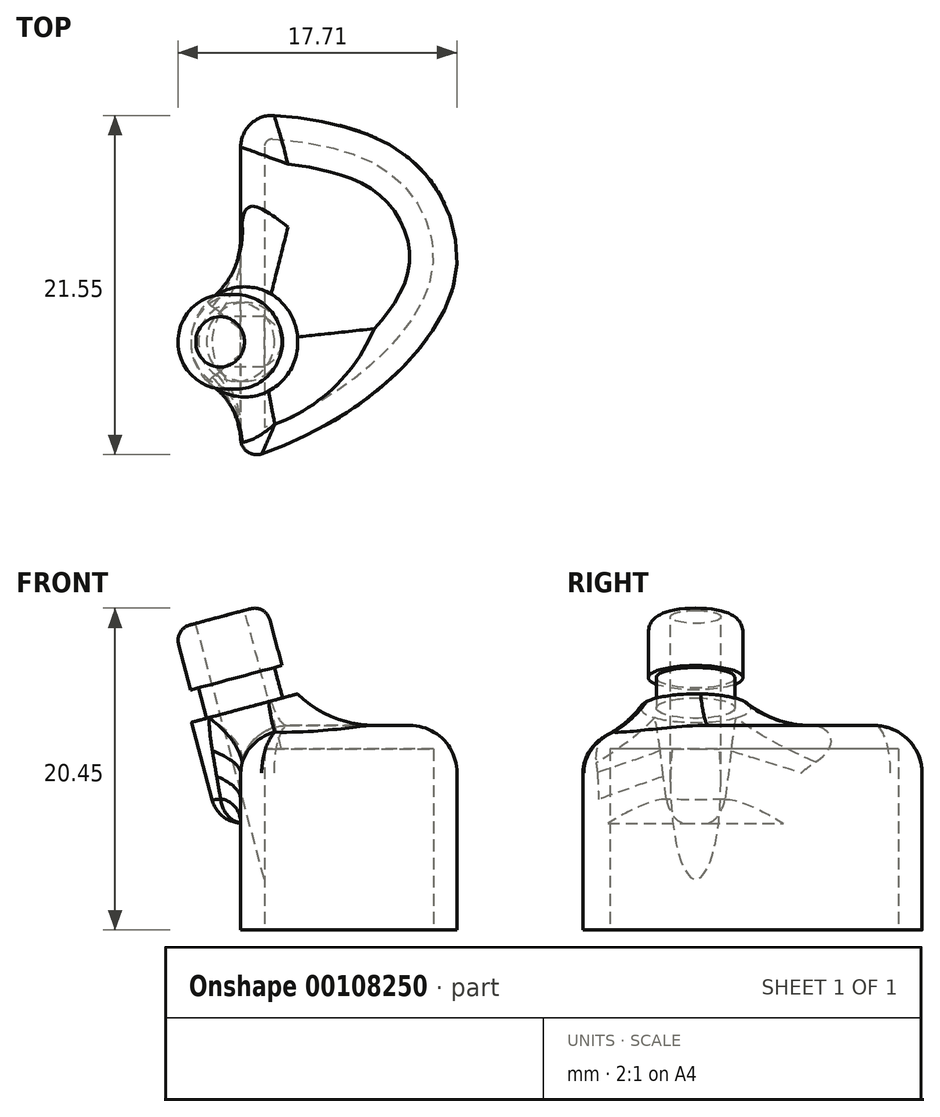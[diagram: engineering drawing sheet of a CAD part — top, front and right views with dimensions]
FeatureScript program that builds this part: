
annotation { "Feature Type Name" : "Feature", "Feature Type Description" : "" }
export const myFeature = defineFeature(function(context is Context, id is Id, definition is map)
    precondition{}
    {
        {
            var Q0;
            Q0=qCreatedBy(makeId("Top.planeOp"),FACE);
            var sketch = newSketch(context, id + "F0", { "sketchPlane" : qUnion([Q0])});
            skLineSegment(sketch, "E0", {"start": v(0, 10.03) * mm, "end": v(0, -11.97) * mm});
            skFitSpline(sketch, "E1", {"points": [v(0, 10.03) * mm, v(10.47, 7.41) * mm, v(13.67, 0) * mm, v(8.71, -7.47) * mm, v(0, -11.97) * mm], "startDerivative": vector(40.6, -0.18) * mm, "endDerivative": vector(-39.36, -12.15) * mm});
            skSolve(sketch);
        }
        {
            var Q0;
            Q0=makeQuery(id+"F0.imprint","IMPRINT",FACE,{"disambiguationData":[TD([[makeQuery(id+"F0.imprint","IMPRINT",EDGE,{"derivedFrom":sQuery(id+"F0.wireOp",EDGE,"E0")}),1.0]])]});
            extrude(context, id + "F1", {"entities" : qUnion([Q0]), "depth" : 13 * mm});
        }
        {
            var Q0;
            {var subQ0=sQuery(id+"F0.wireOp",EDGE,"E1");var subQ1=sQuery(id+"F0.wireOp",EDGE,"E0");Q0=makeQuery(id+"F1.opExtrude","SWEPT_EDGE",EDGE,{"disambiguationData":[OSD([subQ1,subQ0]),TDD([makeQuery(id+"F0.imprint","INTERSECT",VERTEX,{"disambiguationData":[OD(0.0)],"derivedFrom":[subQ1,subQ0]})])]});}
            fillet(context, id + "F2", {"entities" : qUnion([Q0]), "radius" : 2 * mm, "tangentPropagation" : true, "allowEdgeOverflow" : false});
        }
        {
            var Q0;
            {var subQ0=sQuery(id+"F0.wireOp",EDGE,"E1");var subQ1=sQuery(id+"F0.wireOp",EDGE,"E0");Q0=makeQuery(id+"F1.opExtrude","SWEPT_EDGE",EDGE,{"disambiguationData":[OSD([subQ1,subQ0]),TDD([makeQuery(id+"F0.imprint","INTERSECT",VERTEX,{"disambiguationData":[OD(1.0)],"derivedFrom":[subQ1,subQ0]})])]});}
            fillet(context, id + "F3", {"entities" : qUnion([Q0]), "radius" : 1 * mm, "tangentPropagation" : true, "allowEdgeOverflow" : false});
        }
        {
            var Q0;
            Q0=makeQuery(id+"F1.opExtrude","CAP_FACE",FACE,{"disambiguationData":[OSD([sQuery(id+"F0.wireOp",EDGE,"E0"),sQuery(id+"F0.wireOp",EDGE,"E1")])],"isStart":false});
            var Q1;
            Q1=makeQuery(id+"F1.opExtrude","CAP_EDGE",EDGE,{"disambiguationData":[OSD([sQuery(id+"F0.wireOp",EDGE,"E0")])],"isStart":false});
            cPlane(context, id + "F4", {"entities" : qUnion([Q0, Q1]), "cplaneType" : CPlaneType.LINE_ANGLE, "offset" : 25 * mm, "angle" : 15 * degree, "width" : 150 * mm, "height" : 150 * mm});
        }
        {
            var Q0;
            Q0=makeQuery(id+"F1.opExtrude","CAP_FACE",FACE,{"disambiguationData":[OSD([sQuery(id+"F0.wireOp",EDGE,"E0"),sQuery(id+"F0.wireOp",EDGE,"E1")])],"isStart":true});
            shell(context, id + "F5", {"entities" : qUnion([Q0]), "thickness" : 1.5 * mm});
        }
        {
            var Q0;
            Q0=qCreatedBy(id+"F4.planeOp",FACE);
            var sketch = newSketch(context, id + "F6", { "sketchPlane" : qUnion([Q0])});
            skLineSegment(sketch, "E2", {"start": v(-1.22, 10.68) * mm, "end": v(-1.22, 3.68) * mm});
            skCircle(sketch, "E3", {"center": v(3.89, 4.42) * mm, "radius": 3.5 * mm});
            skSolve(sketch);
        }
        {
            var Q0;
            Q0=makeQuery(id+"F6.imprint","IMPRINT",FACE,{"disambiguationData":[TD([[makeQuery(id+"F6.imprint","IMPRINT",EDGE,{"derivedFrom":sQuery(id+"F6.wireOp",EDGE,"E3")}),1.0]])]});
            extrude(context, id + "F7", {"entities" : qUnion([Q0]), "operationType" : NewBodyOperationType.ADD, "depth" : 6 * mm});
        }
        {
            var Q0;
            Q0=makeQuery(id+"F1.opExtrude","CAP_FACE",FACE,{"disambiguationData":[OSD([sQuery(id+"F0.wireOp",EDGE,"E0"),sQuery(id+"F0.wireOp",EDGE,"E1")])],"isStart":true});
            var sketch = newSketch(context, id + "F8", { "sketchPlane" : qUnion([Q0])});
            skLineSegment(sketch, "E4", {"start": v(1.5, 9.87) * mm, "end": v(1.5, -2.54) * mm});
            skLineSegment(sketch, "E5", {"start": v(1.5, -2.54) * mm, "end": v(10.54, -1.4) * mm});
            skLineSegment(sketch, "E6", {"start": v(10.54, -1.4) * mm, "end": v(8.02, 6.1) * mm});
            skLineSegment(sketch, "E7", {"start": v(8.02, 6.1) * mm, "end": v(1.5, 9.87) * mm});
            skSolve(sketch);
        }
        {
            var Q0;
            Q0=makeQuery(id+"F8.imprint","IMPRINT",FACE,{"disambiguationData":[TD([[makeQuery(id+"F8.imprint","IMPRINT",EDGE,{"derivedFrom":sQuery(id+"F8.wireOp",EDGE,"E4")}),-1.0]])]});
            extrude(context, id + "F9", {"entities" : qUnion([Q0]), "operationType" : NewBodyOperationType.REMOVE, "oppositeDirection" : true, "depth" : 11.5 * mm});
        }
        {
            var Q0;
            Q0=makeQuery(id+"F7.opExtrude","CAP_FACE",FACE,{"disambiguationData":[OSD([sQuery(id+"F6.wireOp",EDGE,"E3")])],"isStart":true});
            extrude(context, id + "F10", {"entities" : qUnion([Q0]), "operationType" : NewBodyOperationType.ADD, "depth" : 1 * mm});
        }
        {
            var Q0;
            Q0=makeQuery(id+"F10.opExtrude","CAP_FACE",FACE,{"disambiguationData":[OSD([sQuery(id+"F6.wireOp",EDGE,"E3")])],"isStart":false});
            var sketch = newSketch(context, id + "F11", { "sketchPlane" : qUnion([Q0])});
            skCircle(sketch, "E8", {"center": v(3.89, -4.42) * mm, "radius": 2.5 * mm});
            skSolve(sketch);
        }
        {
            var Q0;
            Q0=makeQuery(id+"F11.imprint","IMPRINT",FACE,{"disambiguationData":[TD([[makeQuery(id+"F11.imprint","IMPRINT",EDGE,{"derivedFrom":sQuery(id+"F11.wireOp",EDGE,"E8")}),1.0]])]});
            extrude(context, id + "F12", {"entities" : qUnion([Q0]), "operationType" : NewBodyOperationType.ADD, "depth" : 2 * mm});
        }
        {
            var Q0;
            Q0=makeQuery(id+"F12.opExtrude","CAP_FACE",FACE,{"disambiguationData":[OSD([sQuery(id+"F11.wireOp",EDGE,"E8")])],"isStart":false});
            var sketch = newSketch(context, id + "F13", { "sketchPlane" : qUnion([Q0])});
            skCircle(sketch, "E9", {"center": v(3.89, -4.42) * mm, "radius": 3 * mm});
            skSolve(sketch);
        }
        {
            var Q0;
            Q0 = qSketchRegion(id + "F13", true);
            extrude(context, id + "F14", {"entities" : qUnion([Q0]), "operationType" : NewBodyOperationType.ADD, "depth" : 4 * mm});
        }
        {
            var Q0;
            Q0=makeQuery(id+"F14.opExtrude","CAP_EDGE",EDGE,{"disambiguationData":[OSD([sQuery(id+"F13.wireOp",EDGE,"E9")])],"isStart":false});
            fillet(context, id + "F15", {"entities" : qUnion([Q0]), "radius" : 1 * mm, "tangentPropagation" : true, "allowEdgeOverflow" : false});
        }
        {
            var Q0;
            Q0=makeQuery(id+"F1.opExtrude","CAP_EDGE",EDGE,{"disambiguationData":[OSD([sQuery(id+"F0.wireOp",EDGE,"E1")])],"isStart":false});
            fillet(context, id + "F16", {"entities" : qUnion([Q0]), "radius" : 3 * mm, "tangentPropagation" : true, "allowEdgeOverflow" : false});
        }
        {
            var Q0;
            Q0=makeQuery(id+"F7.boolean.opBoolean","INTERSECT",EDGE,{"derivedFrom":[makeQuery(id+"F1.opExtrude","CAP_FACE",FACE,{"disambiguationData":[OSD([sQuery(id+"F0.wireOp",EDGE,"E0"),sQuery(id+"F0.wireOp",EDGE,"E1")])],"isStart":false}),makeQuery(id+"F7.opExtrude","SWEPT_FACE",FACE,{"disambiguationData":[OSD([sQuery(id+"F6.wireOp",EDGE,"E3")])]})]});
            fillet(context, id + "F17", {"entities" : qUnion([Q0]), "radius" : 7 * mm, "tangentPropagation" : true, "allowEdgeOverflow" : false});
        }
        {
            var Q0;
            {var subQ0=sQuery(id+"F6.wireOp",EDGE,"E3");Q0=makeQuery(id+"F7.boolean.opBoolean","SPLIT",EDGE,{"disambiguationData":[TD([makeQuery(id+"F1.opExtrude","SWEPT_FACE",FACE,{"disambiguationData":[OSD([sQuery(id+"F0.wireOp",EDGE,"E0")])]})])],"derivedFrom":makeQuery(id+"F7.opExtrude","CAP_EDGE",EDGE,{"disambiguationData":[OSD([subQ0])],"isStart":false})});}
            fillet(context, id + "F18", {"entities" : qUnion([Q0]), "radius" : 2 * mm, "tangentPropagation" : true, "allowEdgeOverflow" : false});
        }
        {
            var Q0;
            Q0=makeQuery(id+"F14.opExtrude","CAP_FACE",FACE,{"disambiguationData":[OSD([sQuery(id+"F13.wireOp",EDGE,"E9")])],"isStart":false});
            var sketch = newSketch(context, id + "F19", { "sketchPlane" : qUnion([Q0])});
            skCircle(sketch, "E10", {"center": v(3.89, -4.42) * mm, "radius": 1.6 * mm});
            skSolve(sketch);
        }
        {
            var Q0;
            Q0=makeQuery(id+"F19.imprint","IMPRINT",FACE,{"disambiguationData":[TD([[makeQuery(id+"F19.imprint","IMPRINT",EDGE,{"derivedFrom":sQuery(id+"F19.wireOp",EDGE,"E10")}),1.0]])]});
            extrude(context, id + "F20", {"entities" : qUnion([Q0]), "operationType" : NewBodyOperationType.REMOVE, "endBound" : BoundingType.THROUGH_ALL, "oppositeDirection" : true, "depth" : 25 * mm});
        }
    });
